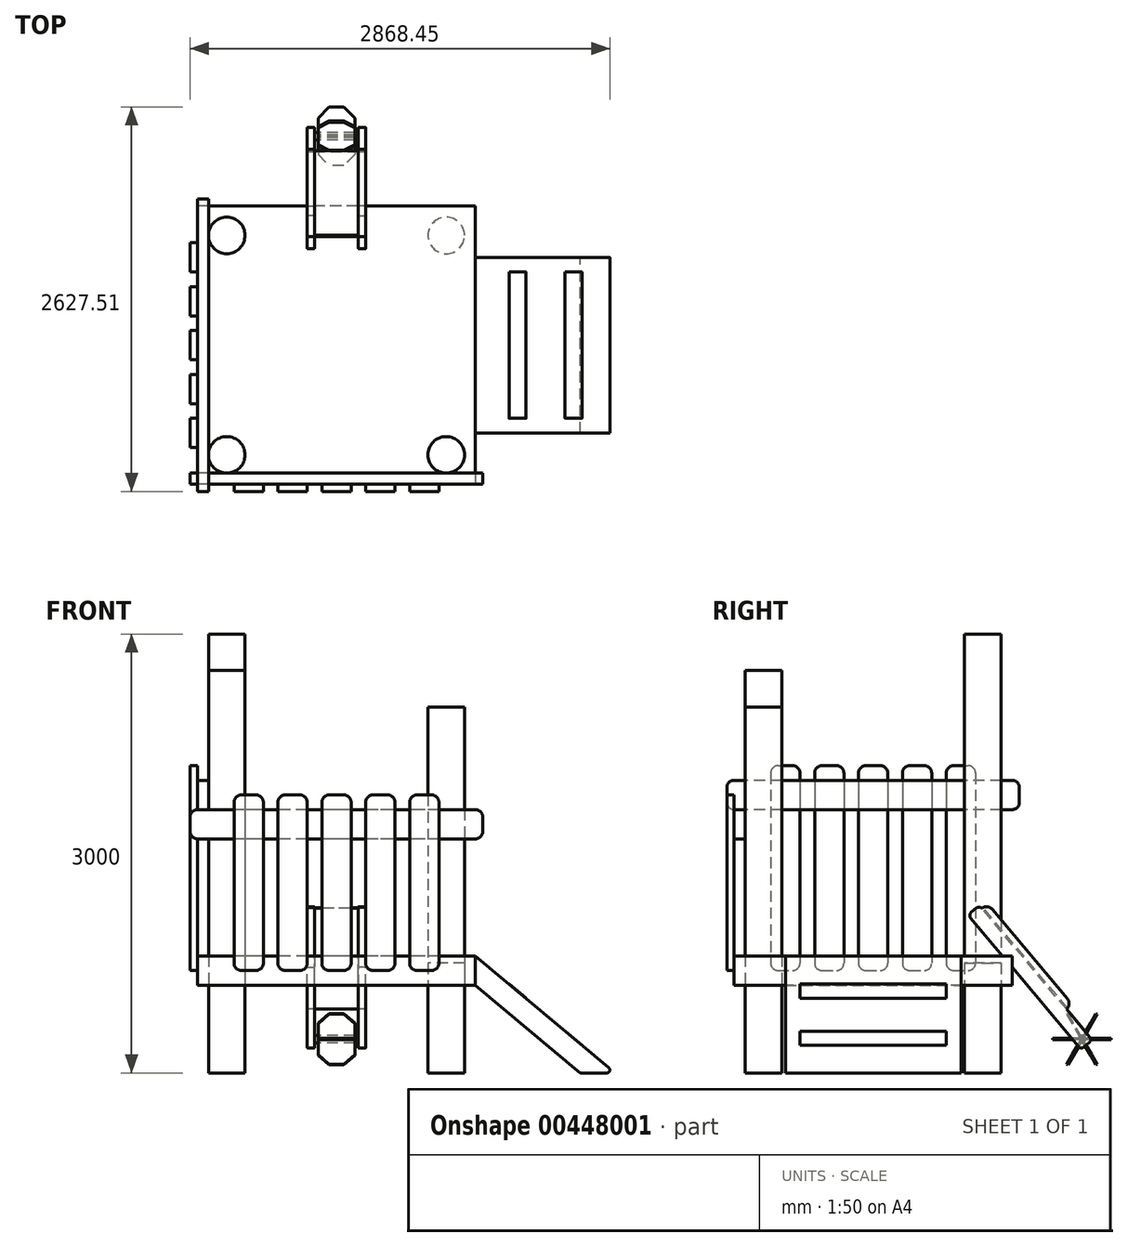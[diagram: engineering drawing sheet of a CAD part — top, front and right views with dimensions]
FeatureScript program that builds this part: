
annotation { "Feature Type Name" : "Feature", "Feature Type Description" : "" }
export const myFeature = defineFeature(function(context is Context, id is Id, definition is map)
    precondition{}
    {
        {
            var Q0;
            Q0=qCreatedBy(makeId("Top.planeOp"),FACE);
            var sketch = newSketch(context, id + "F0", { "sketchPlane" : qUnion([Q0])});
            skLineSegment(sketch, "E0.bottom", {"start": v(750, 750) * mm, "end": v(-750, 750) * mm, "construction": true});
            skLineSegment(sketch, "E0.top", {"start": v(750, -750) * mm, "end": v(-750, -750) * mm, "construction": true});
            skLineSegment(sketch, "E0.left", {"start": v(750, 750) * mm, "end": v(750, -750) * mm, "construction": true});
            skLineSegment(sketch, "E0.right", {"start": v(-750, 750) * mm, "end": v(-750, -750) * mm, "construction": true});
            skPoint(sketch, "E0.middle", {"position": v(0, 0) * mm});
            skCircle(sketch, "E1", {"center": v(-750, 750) * mm, "radius": 125 * mm});
            skCircle(sketch, "E2", {"center": v(750, 750) * mm, "radius": 125 * mm});
            skCircle(sketch, "E3", {"center": v(750, -750) * mm, "radius": 125 * mm});
            skCircle(sketch, "E4", {"center": v(-750, -750) * mm, "radius": 125 * mm});
            skSolve(sketch);
        }
        {
            var Q0;
            Q0=qCreatedBy(makeId("Top.planeOp"),FACE);
            cPlane(context, id + "F1", {"entities" : qUnion([Q0]), "cplaneType" : CPlaneType.OFFSET, "offset" : 800 * mm, "width" : 150 * mm, "height" : 150 * mm});
        }
        {
            var Q0;
            Q0=qCreatedBy(id+"F1.planeOp",FACE);
            var sketch = newSketch(context, id + "F2", { "sketchPlane" : qUnion([Q0])});
            skLineSegment(sketch, "E5.bottom", {"start": v(950, 950) * mm, "end": v(-950, 950) * mm});
            skLineSegment(sketch, "E5.top", {"start": v(950, -950) * mm, "end": v(-950, -950) * mm});
            skLineSegment(sketch, "E5.left", {"start": v(950, 950) * mm, "end": v(950, -950) * mm});
            skLineSegment(sketch, "E5.right", {"start": v(-950, 950) * mm, "end": v(-950, -950) * mm});
            skPoint(sketch, "E5.middle", {"position": v(0, 0) * mm});
            skSolve(sketch);
        }
        {
            var Q0;
            Q0=makeQuery(id+"F0.imprint","IMPRINT",FACE,{"disambiguationData":[TD([[makeQuery(id+"F0.imprint","IMPRINT",EDGE,{"derivedFrom":sQuery(id+"F0.wireOp",EDGE,"E1")}),1.0]])]});
            var Q1;
            Q1=sQuery(id+"F0.wireOp",EDGE,"E1");
            extrude(context, id + "F3", {"entities" : qUnion([Q0]), "surfaceEntities" : qUnion([Q1]), "depth" : 3000 * mm});
        }
        {
            var Q0;
            Q0=makeQuery(id+"F0.imprint","IMPRINT",FACE,{"disambiguationData":[TD([[makeQuery(id+"F0.imprint","IMPRINT",EDGE,{"derivedFrom":sQuery(id+"F0.wireOp",EDGE,"E4")}),1.0]])]});
            var Q1;
            Q1=sQuery(id+"F0.wireOp",EDGE,"E4");
            extrude(context, id + "F4", {"entities" : qUnion([Q0]), "surfaceEntities" : qUnion([Q1]), "depth" : 2750 * mm});
        }
        {
            var Q0;
            Q0=makeQuery(id+"F0.imprint","IMPRINT",FACE,{"disambiguationData":[TD([[makeQuery(id+"F0.imprint","IMPRINT",EDGE,{"derivedFrom":sQuery(id+"F0.wireOp",EDGE,"E3")}),1.0]])]});
            extrude(context, id + "F5", {"entities" : qUnion([Q0]), "depth" : 2500 * mm});
        }
        {
            var Q0;
            Q0=makeQuery(id+"F0.imprint","IMPRINT",FACE,{"disambiguationData":[TD([[makeQuery(id+"F0.imprint","IMPRINT",EDGE,{"derivedFrom":sQuery(id+"F0.wireOp",EDGE,"E2")}),1.0]])]});
            var Q1;
            Q1=sQuery(id+"F0.wireOp",EDGE,"E2");
            extrude(context, id + "F6", {"entities" : qUnion([Q0]), "surfaceEntities" : qUnion([Q1]), "depth" : 750 * mm});
        }
        {
            var Q0;
            Q0=makeQuery(id+"F2.imprint","IMPRINT",FACE,{"disambiguationData":[TD([[makeQuery(id+"F2.imprint","IMPRINT",EDGE,{"derivedFrom":sQuery(id+"F2.wireOp",EDGE,"E5.bottom")}),1.0]])]});
            extrude(context, id + "F7", {"entities" : qUnion([Q0]), "oppositeDirection" : true, "depth" : 200 * mm});
        }
        {
            var Q0;
            Q0=makeQuery(id+"F2.imprint","IMPRINT",FACE,{"disambiguationData":[TD([[makeQuery(id+"F2.imprint","IMPRINT",EDGE,{"derivedFrom":sQuery(id+"F2.wireOp",EDGE,"E5.bottom")}),1.0]])]});
            cPlane(context, id + "F8", {"entities" : qUnion([Q0]), "cplaneType" : CPlaneType.OFFSET, "offset" : 1000 * mm, "width" : 150 * mm, "height" : 150 * mm});
        }
        {
            var Q0;
            Q0=qCreatedBy(id+"F8.planeOp",FACE);
            var sketch = newSketch(context, id + "F9", { "sketchPlane" : qUnion([Q0])});
            skLineSegment(sketch, "E6.bottom", {"start": v(1000, -950) * mm, "end": v(-1000, -950) * mm});
            skLineSegment(sketch, "E6.top", {"start": v(1000, -875) * mm, "end": v(-1000, -875) * mm});
            skLineSegment(sketch, "E6.left", {"start": v(1000, -950) * mm, "end": v(1000, -875) * mm});
            skLineSegment(sketch, "E6.right", {"start": v(-1000, -950) * mm, "end": v(-1000, -875) * mm});
            skPoint(sketch, "E6.middle", {"position": v(0, -912.5) * mm});
            skLineSegment(sketch, "E7.bottom", {"start": v(-950, 1000) * mm, "end": v(-875, 1000) * mm});
            skLineSegment(sketch, "E7.top", {"start": v(-950, -1000) * mm, "end": v(-875, -1000) * mm});
            skLineSegment(sketch, "E7.left", {"start": v(-950, 1000) * mm, "end": v(-950, -1000) * mm});
            skLineSegment(sketch, "E7.right", {"start": v(-875, 1000) * mm, "end": v(-875, -1000) * mm});
            skPoint(sketch, "E7.middle", {"position": v(-912.5, 0) * mm});
            skSolve(sketch);
        }
        {
            var Q0;
            {var subQ5=sQuery(id+"F9.wireOp",EDGE,"E7.bottom");Q0=makeQuery(id+"F9.imprint","IMPRINT",FACE,{"disambiguationData":[TD([[makeQuery(id+"F9.imprint","IMPRINT",EDGE,{"derivedFrom":subQ5}),-1.0]])]});}
            var Q1;
            {var subQ0=sQuery(id+"F9.wireOp",EDGE,"E7.right");var subQ1=sQuery(id+"F9.wireOp",EDGE,"E6.bottom");var subQ2=makeQuery(id+"F9.imprint","INTERSECT",VERTEX,{"derivedFrom":[subQ1,subQ0]});Q1=makeQuery(id+"F9.imprint","IMPRINT",FACE,{"disambiguationData":[TD([[makeQuery(id+"F9.imprint","IMPRINT",EDGE,{"disambiguationData":[TD([[subQ2,-1.0]])],"derivedFrom":subQ1}),-1.0]])]});}
            var Q2;
            {var subQ5=sQuery(id+"F9.wireOp",EDGE,"E7.top");Q2=makeQuery(id+"F9.imprint","IMPRINT",FACE,{"disambiguationData":[TD([[makeQuery(id+"F9.imprint","IMPRINT",EDGE,{"derivedFrom":subQ5}),1.0]])]});}
            extrude(context, id + "F10", {"entities" : qUnion([Q0, Q1, Q2]), "operationType" : NewBodyOperationType.ADD, "depth" : 200 * mm});
        }
        {
            var Q0;
            {var subQ0=sQuery(id+"F9.wireOp",EDGE,"E6.right");Q0=makeQuery(id+"F9.imprint","IMPRINT",FACE,{"disambiguationData":[TD([[makeQuery(id+"F9.imprint","IMPRINT",EDGE,{"derivedFrom":subQ0}),-1.0]])]});}
            var Q1;
            {var subQ0=sQuery(id+"F9.wireOp",EDGE,"E7.right");var subQ1=sQuery(id+"F9.wireOp",EDGE,"E6.bottom");var subQ2=makeQuery(id+"F9.imprint","INTERSECT",VERTEX,{"derivedFrom":[subQ1,subQ0]});Q1=makeQuery(id+"F9.imprint","IMPRINT",FACE,{"disambiguationData":[TD([[makeQuery(id+"F9.imprint","IMPRINT",EDGE,{"disambiguationData":[TD([[subQ2,-1.0]])],"derivedFrom":subQ1}),-1.0]])]});}
            var Q2;
            {var subQ0=sQuery(id+"F9.wireOp",EDGE,"E6.left");Q2=makeQuery(id+"F9.imprint","IMPRINT",FACE,{"disambiguationData":[TD([[makeQuery(id+"F9.imprint","IMPRINT",EDGE,{"derivedFrom":subQ0}),1.0]])]});}
            extrude(context, id + "F11", {"entities" : qUnion([Q0, Q1, Q2]), "depth" : -200 * mm});
        }
        {
            var Q0;
            Q0=makeQuery(id+"F2.imprint","IMPRINT",FACE,{"disambiguationData":[TD([[makeQuery(id+"F2.imprint","IMPRINT",EDGE,{"derivedFrom":sQuery(id+"F2.wireOp",EDGE,"E5.bottom")}),1.0]])]});
            cPlane(context, id + "F12", {"entities" : qUnion([Q0]), "cplaneType" : CPlaneType.OFFSET, "offset" : 500 * mm, "width" : 150 * mm, "height" : 150 * mm});
        }
        {
            var Q0;
            Q0=qCreatedBy(id+"F12.planeOp",FACE);
            var Q1;
            Q1=qCreatedBy(id+"F12.planeOp",FACE);
            var sketch = newSketch(context, id + "F13", { "sketchPlane" : qUnion([Q0, Q1])});
            skLineSegment(sketch, "E8.bottom", {"start": v(100, -1000) * mm, "end": v(-100, -1000) * mm});
            skLineSegment(sketch, "E8.top", {"start": v(100, -950) * mm, "end": v(-100, -950) * mm});
            skLineSegment(sketch, "E8.left", {"start": v(100, -1000) * mm, "end": v(100, -950) * mm});
            skLineSegment(sketch, "E8.right", {"start": v(-100, -1000) * mm, "end": v(-100, -950) * mm});
            skPoint(sketch, "E8.middle", {"position": v(0, -950) * mm});
            skLineSegment(sketch, "E9.1.0.0", {"start": v(400, -1000) * mm, "end": v(400, -950) * mm});
            skLineSegment(sketch, "E9.1.0.1", {"start": v(400, -950) * mm, "end": v(200, -950) * mm});
            skLineSegment(sketch, "E9.1.0.2", {"start": v(400, -1000) * mm, "end": v(200, -1000) * mm});
            skPoint(sketch, "E9.1.0.3", {"position": v(300, -950) * mm});
            skLineSegment(sketch, "E9.1.0.4", {"start": v(200, -1000) * mm, "end": v(200, -950) * mm});
            skLineSegment(sketch, "E9.2.0.0", {"start": v(700, -1000) * mm, "end": v(700, -950) * mm});
            skLineSegment(sketch, "E9.2.0.1", {"start": v(700, -950) * mm, "end": v(500, -950) * mm});
            skLineSegment(sketch, "E9.2.0.2", {"start": v(700, -1000) * mm, "end": v(500, -1000) * mm});
            skPoint(sketch, "E9.2.0.3", {"position": v(600, -950) * mm});
            skLineSegment(sketch, "E9.2.0.4", {"start": v(500, -1000) * mm, "end": v(500, -950) * mm});
            skLineSegment(sketch, "E9.direction1", {"start": v(-100, -1000) * mm, "end": v(200, -1000) * mm, "construction": true});
            skLineSegment(sketch, "E10.1.0.0", {"start": v(-200, -1000) * mm, "end": v(-400, -1000) * mm});
            skLineSegment(sketch, "E10.1.0.1", {"start": v(-200, -950) * mm, "end": v(-400, -950) * mm});
            skLineSegment(sketch, "E10.1.0.2", {"start": v(-200, -1000) * mm, "end": v(-200, -950) * mm});
            skLineSegment(sketch, "E10.1.0.3", {"start": v(-400, -1000) * mm, "end": v(-400, -950) * mm});
            skPoint(sketch, "E10.1.0.4", {"position": v(-300, -950) * mm});
            skLineSegment(sketch, "E10.2.0.0", {"start": v(-500, -1000) * mm, "end": v(-700, -1000) * mm});
            skLineSegment(sketch, "E10.2.0.1", {"start": v(-500, -950) * mm, "end": v(-700, -950) * mm});
            skLineSegment(sketch, "E10.2.0.2", {"start": v(-500, -1000) * mm, "end": v(-500, -950) * mm});
            skLineSegment(sketch, "E10.2.0.3", {"start": v(-700, -1000) * mm, "end": v(-700, -950) * mm});
            skPoint(sketch, "E10.2.0.4", {"position": v(-600, -950) * mm});
            skLineSegment(sketch, "E10.direction1", {"start": v(-100, -1000) * mm, "end": v(-400, -1000) * mm, "construction": true});
            skSolve(sketch);
        }
        {
            var Q0;
            Q0=makeQuery(id+"F13.imprint","IMPRINT",FACE,{"disambiguationData":[TD([[makeQuery(id+"F13.imprint","IMPRINT",EDGE,{"derivedFrom":sQuery(id+"F13.wireOp",EDGE,"E10.2.0.0")}),-1.0]])]});
            var Q1;
            Q1=makeQuery(id+"F13.imprint","IMPRINT",FACE,{"disambiguationData":[TD([[makeQuery(id+"F13.imprint","IMPRINT",EDGE,{"derivedFrom":sQuery(id+"F13.wireOp",EDGE,"E10.1.0.0")}),-1.0]])]});
            var Q2;
            Q2=makeQuery(id+"F13.imprint","IMPRINT",FACE,{"disambiguationData":[TD([[makeQuery(id+"F13.imprint","IMPRINT",EDGE,{"derivedFrom":sQuery(id+"F13.wireOp",EDGE,"E8.bottom")}),-1.0]])]});
            var Q3;
            Q3=makeQuery(id+"F13.imprint","IMPRINT",FACE,{"disambiguationData":[TD([[makeQuery(id+"F13.imprint","IMPRINT",EDGE,{"derivedFrom":sQuery(id+"F13.wireOp",EDGE,"E9.1.0.0")}),1.0]])]});
            var Q4;
            Q4=makeQuery(id+"F13.imprint","IMPRINT",FACE,{"disambiguationData":[TD([[makeQuery(id+"F13.imprint","IMPRINT",EDGE,{"derivedFrom":sQuery(id+"F13.wireOp",EDGE,"E9.2.0.0")}),1.0]])]});
            extrude(context, id + "F14", {"entities" : qUnion([Q0, Q1, Q2, Q3, Q4]), "operationType" : NewBodyOperationType.ADD, "endBound" : BoundingType.SYMMETRIC, "depth" : 1200 * mm});
        }
        {
            var Q0;
            Q0=makeQuery(id+"F2.imprint","IMPRINT",FACE,{"disambiguationData":[TD([[makeQuery(id+"F2.imprint","IMPRINT",EDGE,{"derivedFrom":sQuery(id+"F2.wireOp",EDGE,"E5.bottom")}),1.0]])]});
            cPlane(context, id + "F15", {"entities" : qUnion([Q0]), "cplaneType" : CPlaneType.OFFSET, "offset" : 600 * mm, "width" : 150 * mm, "height" : 150 * mm});
        }
        {
            var Q0;
            Q0=qCreatedBy(id+"F15.planeOp",FACE);
            var sketch = newSketch(context, id + "F16", { "sketchPlane" : qUnion([Q0])});
            skLineSegment(sketch, "E11.bottom", {"start": v(-1000, -100) * mm, "end": v(-950, -100) * mm});
            skLineSegment(sketch, "E11.top", {"start": v(-1000, 100) * mm, "end": v(-950, 100) * mm});
            skLineSegment(sketch, "E11.left", {"start": v(-1000, -100) * mm, "end": v(-1000, 100) * mm});
            skLineSegment(sketch, "E11.right", {"start": v(-950, -100) * mm, "end": v(-950, 100) * mm});
            skPoint(sketch, "E11.middle", {"position": v(-975, 0) * mm});
            skLineSegment(sketch, "E12.0.1.0", {"start": v(-1000, 400) * mm, "end": v(-950, 400) * mm});
            skPoint(sketch, "E12.0.1.1", {"position": v(-975, 300) * mm});
            skLineSegment(sketch, "E12.0.1.2", {"start": v(-1000, 200) * mm, "end": v(-950, 200) * mm});
            skLineSegment(sketch, "E12.0.1.3", {"start": v(-950, 200) * mm, "end": v(-950, 400) * mm});
            skLineSegment(sketch, "E12.0.1.4", {"start": v(-1000, 200) * mm, "end": v(-1000, 400) * mm});
            skLineSegment(sketch, "E12.0.2.0", {"start": v(-1000, 700) * mm, "end": v(-950, 700) * mm});
            skPoint(sketch, "E12.0.2.1", {"position": v(-975, 600) * mm});
            skLineSegment(sketch, "E12.0.2.2", {"start": v(-1000, 500) * mm, "end": v(-950, 500) * mm});
            skLineSegment(sketch, "E12.0.2.3", {"start": v(-950, 500) * mm, "end": v(-950, 700) * mm});
            skLineSegment(sketch, "E12.0.2.4", {"start": v(-1000, 500) * mm, "end": v(-1000, 700) * mm});
            skLineSegment(sketch, "E12.direction1", {"start": v(-1000, -100) * mm, "end": v(-975, -100) * mm, "construction": true});
            skLineSegment(sketch, "E12.direction2", {"start": v(-1000, -100) * mm, "end": v(-1000, 200) * mm, "construction": true});
            skPoint(sketch, "E13.0.1.0", {"position": v(-975, -300) * mm});
            skLineSegment(sketch, "E13.0.1.1", {"start": v(-950, -400) * mm, "end": v(-950, -200) * mm});
            skLineSegment(sketch, "E13.0.1.2", {"start": v(-1000, -400) * mm, "end": v(-1000, -200) * mm});
            skLineSegment(sketch, "E13.0.1.3", {"start": v(-1000, -200) * mm, "end": v(-950, -200) * mm});
            skLineSegment(sketch, "E13.0.1.4", {"start": v(-1000, -400) * mm, "end": v(-975, -400) * mm, "construction": true});
            skLineSegment(sketch, "E13.0.1.5", {"start": v(-1000, -400) * mm, "end": v(-950, -400) * mm});
            skPoint(sketch, "E13.0.2.0", {"position": v(-975, -600) * mm});
            skLineSegment(sketch, "E13.0.2.1", {"start": v(-950, -700) * mm, "end": v(-950, -500) * mm});
            skLineSegment(sketch, "E13.0.2.2", {"start": v(-1000, -700) * mm, "end": v(-1000, -500) * mm});
            skLineSegment(sketch, "E13.0.2.3", {"start": v(-1000, -500) * mm, "end": v(-950, -500) * mm});
            skLineSegment(sketch, "E13.0.2.4", {"start": v(-1000, -700) * mm, "end": v(-975, -700) * mm, "construction": true});
            skLineSegment(sketch, "E13.0.2.5", {"start": v(-1000, -700) * mm, "end": v(-950, -700) * mm});
            skLineSegment(sketch, "E13.direction2", {"start": v(-1000, -100) * mm, "end": v(-1000, -400) * mm, "construction": true});
            skSolve(sketch);
        }
        {
            var Q0;
            Q0=makeQuery(id+"F16.imprint","IMPRINT",FACE,{"disambiguationData":[TD([[makeQuery(id+"F16.imprint","IMPRINT",EDGE,{"derivedFrom":sQuery(id+"F16.wireOp",EDGE,"E13.0.2.1")}),1.0]])]});
            var Q1;
            Q1=makeQuery(id+"F16.imprint","IMPRINT",FACE,{"disambiguationData":[TD([[makeQuery(id+"F16.imprint","IMPRINT",EDGE,{"derivedFrom":sQuery(id+"F16.wireOp",EDGE,"E13.0.1.1")}),1.0]])]});
            var Q2;
            Q2=makeQuery(id+"F16.imprint","IMPRINT",FACE,{"disambiguationData":[TD([[makeQuery(id+"F16.imprint","IMPRINT",EDGE,{"derivedFrom":sQuery(id+"F16.wireOp",EDGE,"E11.bottom")}),1.0]])]});
            var Q3;
            Q3=makeQuery(id+"F16.imprint","IMPRINT",FACE,{"disambiguationData":[TD([[makeQuery(id+"F16.imprint","IMPRINT",EDGE,{"derivedFrom":sQuery(id+"F16.wireOp",EDGE,"E12.0.2.0")}),-1.0]])]});
            var Q4;
            Q4=makeQuery(id+"F16.imprint","IMPRINT",FACE,{"disambiguationData":[TD([[makeQuery(id+"F16.imprint","IMPRINT",EDGE,{"derivedFrom":sQuery(id+"F16.wireOp",EDGE,"E12.0.1.0")}),-1.0]])]});
            extrude(context, id + "F17", {"entities" : qUnion([Q0, Q1, Q2, Q3, Q4]), "endBound" : BoundingType.SYMMETRIC, "depth" : 1400 * mm});
        }
        {
            var Q0;
            Q0=makeQuery(id+"F10.opExtrude","CAP_EDGE",EDGE,{"disambiguationData":[OSD([sQuery(id+"F9.wireOp",EDGE,"E7.top")])],"isStart":false});
            var Q1;
            Q1=makeQuery(id+"F10.opExtrude","CAP_EDGE",EDGE,{"disambiguationData":[OSD([sQuery(id+"F9.wireOp",EDGE,"E7.top")])],"isStart":true});
            var Q2;
            Q2=makeQuery(id+"F10.opExtrude","CAP_EDGE",EDGE,{"disambiguationData":[OSD([sQuery(id+"F9.wireOp",EDGE,"E7.bottom")])],"isStart":false});
            var Q3;
            Q3=makeQuery(id+"F10.opExtrude","CAP_EDGE",EDGE,{"disambiguationData":[OSD([sQuery(id+"F9.wireOp",EDGE,"E7.bottom")])],"isStart":true});
            var Q4;
            Q4=makeQuery(id+"F11.opExtrude","CAP_EDGE",EDGE,{"disambiguationData":[OSD([sQuery(id+"F9.wireOp",EDGE,"E6.right")])],"isStart":true});
            var Q5;
            Q5=makeQuery(id+"F11.opExtrude","CAP_EDGE",EDGE,{"disambiguationData":[OSD([sQuery(id+"F9.wireOp",EDGE,"E6.right")])],"isStart":false});
            var Q6;
            Q6=makeQuery(id+"F11.opExtrude","CAP_EDGE",EDGE,{"disambiguationData":[OSD([sQuery(id+"F9.wireOp",EDGE,"E6.left")])],"isStart":true});
            var Q7;
            Q7=makeQuery(id+"F11.opExtrude","CAP_EDGE",EDGE,{"disambiguationData":[OSD([sQuery(id+"F9.wireOp",EDGE,"E6.left")])],"isStart":false});
            var Q8;
            Q8=makeQuery(id+"F14.opExtrude","CAP_EDGE",EDGE,{"disambiguationData":[OSD([sQuery(id+"F13.wireOp",EDGE,"E10.2.0.3")])],"isStart":false});
            var Q9;
            Q9=makeQuery(id+"F14.opExtrude","CAP_EDGE",EDGE,{"disambiguationData":[OSD([sQuery(id+"F13.wireOp",EDGE,"E10.2.0.2")])],"isStart":false});
            var Q10;
            Q10=makeQuery(id+"F14.opExtrude","CAP_EDGE",EDGE,{"disambiguationData":[OSD([sQuery(id+"F13.wireOp",EDGE,"E10.1.0.3")])],"isStart":false});
            var Q11;
            Q11=makeQuery(id+"F14.opExtrude","CAP_EDGE",EDGE,{"disambiguationData":[OSD([sQuery(id+"F13.wireOp",EDGE,"E10.1.0.2")])],"isStart":false});
            var Q12;
            Q12=makeQuery(id+"F14.opExtrude","CAP_EDGE",EDGE,{"disambiguationData":[OSD([sQuery(id+"F13.wireOp",EDGE,"E8.right")])],"isStart":false});
            var Q13;
            Q13=makeQuery(id+"F14.opExtrude","CAP_EDGE",EDGE,{"disambiguationData":[OSD([sQuery(id+"F13.wireOp",EDGE,"E8.left")])],"isStart":false});
            var Q14;
            Q14=makeQuery(id+"F14.opExtrude","CAP_EDGE",EDGE,{"disambiguationData":[OSD([sQuery(id+"F13.wireOp",EDGE,"E9.1.0.4")])],"isStart":false});
            var Q15;
            Q15=makeQuery(id+"F14.opExtrude","CAP_EDGE",EDGE,{"disambiguationData":[OSD([sQuery(id+"F13.wireOp",EDGE,"E9.1.0.0")])],"isStart":false});
            var Q16;
            Q16=makeQuery(id+"F14.opExtrude","CAP_EDGE",EDGE,{"disambiguationData":[OSD([sQuery(id+"F13.wireOp",EDGE,"E9.2.0.4")])],"isStart":false});
            var Q17;
            Q17=makeQuery(id+"F14.opExtrude","CAP_EDGE",EDGE,{"disambiguationData":[OSD([sQuery(id+"F13.wireOp",EDGE,"E9.2.0.0")])],"isStart":false});
            var Q18;
            Q18=makeQuery(id+"F14.opExtrude","CAP_EDGE",EDGE,{"disambiguationData":[OSD([sQuery(id+"F13.wireOp",EDGE,"E10.2.0.3")])],"isStart":true});
            var Q19;
            Q19=makeQuery(id+"F14.opExtrude","CAP_EDGE",EDGE,{"disambiguationData":[OSD([sQuery(id+"F13.wireOp",EDGE,"E10.2.0.2")])],"isStart":true});
            var Q20;
            Q20=makeQuery(id+"F14.opExtrude","CAP_EDGE",EDGE,{"disambiguationData":[OSD([sQuery(id+"F13.wireOp",EDGE,"E10.1.0.3")])],"isStart":true});
            var Q21;
            Q21=makeQuery(id+"F14.opExtrude","CAP_EDGE",EDGE,{"disambiguationData":[OSD([sQuery(id+"F13.wireOp",EDGE,"E10.1.0.2")])],"isStart":true});
            var Q22;
            Q22=makeQuery(id+"F14.opExtrude","CAP_EDGE",EDGE,{"disambiguationData":[OSD([sQuery(id+"F13.wireOp",EDGE,"E8.right")])],"isStart":true});
            var Q23;
            Q23=makeQuery(id+"F14.opExtrude","CAP_EDGE",EDGE,{"disambiguationData":[OSD([sQuery(id+"F13.wireOp",EDGE,"E8.left")])],"isStart":true});
            var Q24;
            Q24=makeQuery(id+"F14.opExtrude","CAP_EDGE",EDGE,{"disambiguationData":[OSD([sQuery(id+"F13.wireOp",EDGE,"E9.1.0.4")])],"isStart":true});
            var Q25;
            Q25=makeQuery(id+"F14.opExtrude","CAP_EDGE",EDGE,{"disambiguationData":[OSD([sQuery(id+"F13.wireOp",EDGE,"E9.1.0.0")])],"isStart":true});
            var Q26;
            Q26=makeQuery(id+"F14.opExtrude","CAP_EDGE",EDGE,{"disambiguationData":[OSD([sQuery(id+"F13.wireOp",EDGE,"E9.2.0.4")])],"isStart":true});
            var Q27;
            Q27=makeQuery(id+"F14.opExtrude","CAP_EDGE",EDGE,{"disambiguationData":[OSD([sQuery(id+"F13.wireOp",EDGE,"E9.2.0.0")])],"isStart":true});
            var Q28;
            Q28=makeQuery(id+"F17.opExtrude","CAP_EDGE",EDGE,{"disambiguationData":[OSD([sQuery(id+"F16.wireOp",EDGE,"E12.0.2.0")])],"isStart":false});
            var Q29;
            Q29=makeQuery(id+"F17.opExtrude","CAP_EDGE",EDGE,{"disambiguationData":[OSD([sQuery(id+"F16.wireOp",EDGE,"E12.0.2.2")])],"isStart":false});
            var Q30;
            Q30=makeQuery(id+"F17.opExtrude","CAP_EDGE",EDGE,{"disambiguationData":[OSD([sQuery(id+"F16.wireOp",EDGE,"E12.0.1.0")])],"isStart":false});
            var Q31;
            Q31=makeQuery(id+"F17.opExtrude","CAP_EDGE",EDGE,{"disambiguationData":[OSD([sQuery(id+"F16.wireOp",EDGE,"E12.0.1.2")])],"isStart":false});
            var Q32;
            Q32=makeQuery(id+"F17.opExtrude","CAP_EDGE",EDGE,{"disambiguationData":[OSD([sQuery(id+"F16.wireOp",EDGE,"E11.top")])],"isStart":false});
            var Q33;
            Q33=makeQuery(id+"F17.opExtrude","CAP_EDGE",EDGE,{"disambiguationData":[OSD([sQuery(id+"F16.wireOp",EDGE,"E11.bottom")])],"isStart":false});
            var Q34;
            Q34=makeQuery(id+"F17.opExtrude","CAP_EDGE",EDGE,{"disambiguationData":[OSD([sQuery(id+"F16.wireOp",EDGE,"E13.0.1.3")])],"isStart":false});
            var Q35;
            Q35=makeQuery(id+"F17.opExtrude","CAP_EDGE",EDGE,{"disambiguationData":[OSD([sQuery(id+"F16.wireOp",EDGE,"E13.0.1.5")])],"isStart":false});
            var Q36;
            Q36=makeQuery(id+"F17.opExtrude","CAP_EDGE",EDGE,{"disambiguationData":[OSD([sQuery(id+"F16.wireOp",EDGE,"E13.0.2.3")])],"isStart":false});
            var Q37;
            Q37=makeQuery(id+"F17.opExtrude","CAP_EDGE",EDGE,{"disambiguationData":[OSD([sQuery(id+"F16.wireOp",EDGE,"E13.0.2.5")])],"isStart":false});
            var Q38;
            Q38=makeQuery(id+"F17.opExtrude","CAP_EDGE",EDGE,{"disambiguationData":[OSD([sQuery(id+"F16.wireOp",EDGE,"E13.0.2.5")])],"isStart":true});
            var Q39;
            Q39=makeQuery(id+"F17.opExtrude","CAP_EDGE",EDGE,{"disambiguationData":[OSD([sQuery(id+"F16.wireOp",EDGE,"E13.0.2.3")])],"isStart":true});
            var Q40;
            Q40=makeQuery(id+"F17.opExtrude","CAP_EDGE",EDGE,{"disambiguationData":[OSD([sQuery(id+"F16.wireOp",EDGE,"E13.0.1.5")])],"isStart":true});
            var Q41;
            Q41=makeQuery(id+"F17.opExtrude","CAP_EDGE",EDGE,{"disambiguationData":[OSD([sQuery(id+"F16.wireOp",EDGE,"E13.0.1.3")])],"isStart":true});
            var Q42;
            Q42=makeQuery(id+"F17.opExtrude","CAP_EDGE",EDGE,{"disambiguationData":[OSD([sQuery(id+"F16.wireOp",EDGE,"E11.bottom")])],"isStart":true});
            var Q43;
            Q43=makeQuery(id+"F17.opExtrude","CAP_EDGE",EDGE,{"disambiguationData":[OSD([sQuery(id+"F16.wireOp",EDGE,"E11.top")])],"isStart":true});
            var Q44;
            Q44=makeQuery(id+"F17.opExtrude","CAP_EDGE",EDGE,{"disambiguationData":[OSD([sQuery(id+"F16.wireOp",EDGE,"E12.0.1.2")])],"isStart":true});
            var Q45;
            Q45=makeQuery(id+"F17.opExtrude","CAP_EDGE",EDGE,{"disambiguationData":[OSD([sQuery(id+"F16.wireOp",EDGE,"E12.0.1.0")])],"isStart":true});
            var Q46;
            Q46=makeQuery(id+"F17.opExtrude","CAP_EDGE",EDGE,{"disambiguationData":[OSD([sQuery(id+"F16.wireOp",EDGE,"E12.0.2.2")])],"isStart":true});
            var Q47;
            Q47=makeQuery(id+"F17.opExtrude","CAP_EDGE",EDGE,{"disambiguationData":[OSD([sQuery(id+"F16.wireOp",EDGE,"E12.0.2.0")])],"isStart":true});
            fillet(context, id + "F18", {"entities" : qUnion([Q0, Q1, Q2, Q3, Q4, Q5, Q6, Q7, Q8, Q9, Q10, Q11, Q12, Q13, Q14, Q15, Q16, Q17, Q18, Q19, Q20, Q21, Q22, Q23, Q24, Q25, Q26, Q27, Q28, Q29, Q30, Q31, Q32, Q33, Q34, Q35, Q36, Q37, Q38, Q39, Q40, Q41, Q42, Q43, Q44, Q45, Q46, Q47]), "radius" : 50 * mm, "tangentPropagation" : true, "allowEdgeOverflow" : false});
        }
        {
            var Q0;
            Q0=qCreatedBy(makeId("Front.planeOp"),FACE);
            var sketch = newSketch(context, id + "F19", { "sketchPlane" : qUnion([Q0])});
            skLineSegment(sketch, "E14", {"start": v(950, 800) * mm, "end": v(1861.3, 35.32) * mm});
            skLineSegment(sketch, "E15", {"start": v(1848.45, 0) * mm, "end": v(1665.05, 0) * mm});
            skLineSegment(sketch, "E16", {"start": v(1665.05, 0) * mm, "end": v(950, 600) * mm});
            skLineSegment(sketch, "E17", {"start": v(950, 600) * mm, "end": v(950, 800) * mm});
            skPoint(sketch, "E18", {"position": v(950, 800) * mm});
            skPoint(sketch, "E19.visualSharp", {"position": v(1903.4, 0) * mm});
            skArc(sketch, "E19.filletArc", {"start": v(1848.45, 0) * mm, "mid": v(1867.25, 13.16) * mm, "end": v(1861.3, 35.32) * mm});
            skSolve(sketch);
        }
        {
            var Q0;
            Q0=makeQuery(id+"F19.imprint","IMPRINT",FACE,{"disambiguationData":[TD([[makeQuery(id+"F19.imprint","IMPRINT",EDGE,{"derivedFrom":sQuery(id+"F19.wireOp",EDGE,"E14")}),-1.0]])]});
            extrude(context, id + "F20", {"entities" : qUnion([Q0]), "operationType" : NewBodyOperationType.ADD, "endBound" : BoundingType.SYMMETRIC, "depth" : 1200 * mm});
        }
        {
            var Q0;
            Q0=makeQuery(id+"F20.opExtrude","SWEPT_FACE",FACE,{"disambiguationData":[OSD([sQuery(id+"F19.wireOp",EDGE,"E14")])]});
            var sketch = newSketch(context, id + "F21", { "sketchPlane" : qUnion([Q0])});
            skLineSegment(sketch, "E20.bottom", {"start": v(663.51, 500) * mm, "end": v(513.51, 500) * mm});
            skLineSegment(sketch, "E20.top", {"start": v(663.51, -500) * mm, "end": v(513.51, -500) * mm});
            skLineSegment(sketch, "E20.left", {"start": v(663.51, 500) * mm, "end": v(663.51, -500) * mm});
            skLineSegment(sketch, "E20.right", {"start": v(513.51, 500) * mm, "end": v(513.51, -500) * mm});
            skPoint(sketch, "E20.middle", {"position": v(588.51, 0) * mm});
            skLineSegment(sketch, "E21.bottom", {"start": v(1163.51, 500) * mm, "end": v(1013.51, 500) * mm});
            skLineSegment(sketch, "E21.top", {"start": v(1163.51, -500) * mm, "end": v(1013.51, -500) * mm});
            skLineSegment(sketch, "E21.left", {"start": v(1163.51, 500) * mm, "end": v(1163.51, -500) * mm});
            skLineSegment(sketch, "E21.right", {"start": v(1013.51, 500) * mm, "end": v(1013.51, -500) * mm});
            skPoint(sketch, "E21.middle", {"position": v(1088.51, 0) * mm});
            skSolve(sketch);
        }
        {
            var Q0;
            Q0=makeQuery(id+"F21.imprint","IMPRINT",FACE,{"disambiguationData":[TD([[makeQuery(id+"F21.imprint","IMPRINT",EDGE,{"derivedFrom":sQuery(id+"F21.wireOp",EDGE,"E20.bottom")}),1.0]])]});
            var Q1;
            Q1=makeQuery(id+"F21.imprint","IMPRINT",FACE,{"disambiguationData":[TD([[makeQuery(id+"F21.imprint","IMPRINT",EDGE,{"derivedFrom":sQuery(id+"F21.wireOp",EDGE,"E21.bottom")}),1.0]])]});
            extrude(context, id + "F22", {"entities" : qUnion([Q0, Q1]), "operationType" : NewBodyOperationType.ADD, "depth" : 15 / 20 * mm});
        }
        {
            var Q0;
            Q0=makeQuery(id+"F22.opExtrude","CAP_EDGE",EDGE,{"disambiguationData":[OSD([sQuery(id+"F21.wireOp",EDGE,"E20.left")])],"isStart":false});
            var Q1;
            Q1=makeQuery(id+"F22.opExtrude","CAP_EDGE",EDGE,{"disambiguationData":[OSD([sQuery(id+"F21.wireOp",EDGE,"E20.right")])],"isStart":false});
            var Q2;
            Q2=makeQuery(id+"F22.opExtrude","CAP_EDGE",EDGE,{"disambiguationData":[OSD([sQuery(id+"F21.wireOp",EDGE,"E21.right")])],"isStart":false});
            var Q3;
            Q3=makeQuery(id+"F22.opExtrude","CAP_EDGE",EDGE,{"disambiguationData":[OSD([sQuery(id+"F21.wireOp",EDGE,"E21.left")])],"isStart":false});
            fillet(context, id + "F23", {"entities" : qUnion([Q0, Q1, Q2, Q3]), "radius" : 15 / 20 * mm, "tangentPropagation" : true, "allowEdgeOverflow" : false});
        }
        {
            var Q0;
            Q0=qCreatedBy(makeId("Right.planeOp"),FACE);
            cPlane(context, id + "F24", {"entities" : qUnion([Q0]), "cplaneType" : CPlaneType.OFFSET, "offset" : 150 * mm, "width" : 150 * mm, "height" : 150 * mm});
        }
        {
            var Q0;
            Q0=qCreatedBy(makeId("Right.planeOp"),FACE);
            cPlane(context, id + "F25", {"entities" : qUnion([Q0]), "cplaneType" : CPlaneType.OFFSET, "offset" : 150 * mm, "oppositeDirection" : true, "width" : 150 * mm, "height" : 150 * mm});
        }
        {
            var Q0;
            Q0=qCreatedBy(id+"F24.planeOp",FACE);
            var sketch = newSketch(context, id + "F26", { "sketchPlane" : qUnion([Q0])});
            skLineSegment(sketch, "E22.bottom", {"start": v(1421.35, 160.49) * mm, "end": v(650, 1079.74) * mm});
            skLineSegment(sketch, "E22.top", {"start": v(1497.95, 224.77) * mm, "end": v(726.6, 1144.02) * mm});
            skLineSegment(sketch, "E22.left", {"start": v(1421.35, 160.49) * mm, "end": v(1497.95, 224.77) * mm});
            skLineSegment(sketch, "E22.right", {"start": v(650, 1079.74) * mm, "end": v(726.6, 1144.02) * mm});
            skPoint(sketch, "E22.middle", {"position": v(1073.97, 652.25) * mm});
            skSolve(sketch);
        }
        {
            var Q0;
            Q0=qCreatedBy(id+"F25.planeOp",FACE);
            var sketch = newSketch(context, id + "F27", { "sketchPlane" : qUnion([Q0])});
            skLineSegment(sketch, "E23.bottom", {"start": v(1421.35, 160.49) * mm, "end": v(650, 1079.74) * mm});
            skLineSegment(sketch, "E23.top", {"start": v(1497.95, 224.77) * mm, "end": v(726.6, 1144.02) * mm});
            skLineSegment(sketch, "E23.left", {"start": v(1421.35, 160.49) * mm, "end": v(1497.95, 224.77) * mm});
            skLineSegment(sketch, "E23.right", {"start": v(650, 1079.74) * mm, "end": v(726.6, 1144.02) * mm});
            skPoint(sketch, "E23.middle", {"position": v(1073.97, 652.25) * mm});
            skSolve(sketch);
        }
        {
            var Q0;
            Q0=qCreatedBy(makeId("Right.planeOp"),FACE);
            var sketch = newSketch(context, id + "F28", { "sketchPlane" : qUnion([Q0])});
            skLineSegment(sketch, "E24.bottom", {"start": v(1627.5, 225.93) * mm, "end": v(1227.5, 225.93) * mm});
            skLineSegment(sketch, "E24.top", {"start": v(1627.5, 235.93) * mm, "end": v(1227.5, 235.93) * mm});
            skLineSegment(sketch, "E24.left", {"start": v(1627.5, 225.93) * mm, "end": v(1627.5, 235.93) * mm});
            skLineSegment(sketch, "E24.right", {"start": v(1227.5, 225.93) * mm, "end": v(1227.5, 235.93) * mm});
            skPoint(sketch, "E24.middle", {"position": v(1427.5, 230.93) * mm});
            skLineSegment(sketch, "E25.bottom", {"start": v(1523.18, 55.22) * mm, "end": v(1323.18, 401.63) * mm});
            skLineSegment(sketch, "E25.top", {"start": v(1531.84, 60.22) * mm, "end": v(1331.84, 406.63) * mm});
            skLineSegment(sketch, "E25.left", {"start": v(1523.18, 55.22) * mm, "end": v(1531.84, 60.22) * mm});
            skLineSegment(sketch, "E25.right", {"start": v(1323.18, 401.63) * mm, "end": v(1331.84, 406.63) * mm});
            skLineSegment(sketch, "E26.bottom", {"start": v(1531.84, 401.63) * mm, "end": v(1331.84, 55.22) * mm});
            skLineSegment(sketch, "E26.top", {"start": v(1523.18, 406.63) * mm, "end": v(1323.18, 60.22) * mm});
            skLineSegment(sketch, "E26.left", {"start": v(1531.84, 401.63) * mm, "end": v(1523.18, 406.63) * mm});
            skLineSegment(sketch, "E26.right", {"start": v(1331.84, 55.22) * mm, "end": v(1323.18, 60.22) * mm});
            skSolve(sketch);
        }
        {
            var Q0;
            Q0=qCreatedBy(makeId("Right.planeOp"),FACE);
            var sketch = newSketch(context, id + "F29", { "sketchPlane" : qUnion([Q0])});
            skCircle(sketch, "E27", {"center": v(1427.5, 230.93) * mm, "radius": 25 * mm});
            skSolve(sketch);
        }
        {
            var Q0;
            Q0 = qSketchRegion(id + "F28", true);
            extrude(context, id + "F30", {"entities" : qUnion([Q0]), "endBound" : BoundingType.SYMMETRIC, "depth" : 250 * mm});
        }
        {
            var Q0;
            Q0=makeQuery(id+"F30.opExtrude","CAP_EDGE",EDGE,{"disambiguationData":[OSD([sQuery(id+"F28.wireOp",EDGE,"E26.left")])],"isStart":false});
            var Q1;
            Q1=makeQuery(id+"F30.opExtrude","CAP_EDGE",EDGE,{"disambiguationData":[OSD([sQuery(id+"F28.wireOp",EDGE,"E26.left")])],"isStart":true});
            var Q2;
            Q2=makeQuery(id+"F30.opExtrude","CAP_EDGE",EDGE,{"disambiguationData":[OSD([sQuery(id+"F28.wireOp",EDGE,"E24.left")])],"isStart":true});
            var Q3;
            Q3=makeQuery(id+"F30.opExtrude","CAP_EDGE",EDGE,{"disambiguationData":[OSD([sQuery(id+"F28.wireOp",EDGE,"E24.left")])],"isStart":false});
            var Q4;
            Q4=makeQuery(id+"F30.opExtrude","CAP_EDGE",EDGE,{"disambiguationData":[OSD([sQuery(id+"F28.wireOp",EDGE,"E25.left")])],"isStart":false});
            var Q5;
            Q5=makeQuery(id+"F30.opExtrude","CAP_EDGE",EDGE,{"disambiguationData":[OSD([sQuery(id+"F28.wireOp",EDGE,"E25.left")])],"isStart":true});
            var Q6;
            Q6=makeQuery(id+"F30.opExtrude","CAP_EDGE",EDGE,{"disambiguationData":[OSD([sQuery(id+"F28.wireOp",EDGE,"E26.right")])],"isStart":false});
            var Q7;
            Q7=makeQuery(id+"F30.opExtrude","CAP_EDGE",EDGE,{"disambiguationData":[OSD([sQuery(id+"F28.wireOp",EDGE,"E26.right")])],"isStart":true});
            var Q8;
            Q8=makeQuery(id+"F30.opExtrude","CAP_EDGE",EDGE,{"disambiguationData":[OSD([sQuery(id+"F28.wireOp",EDGE,"E24.right")])],"isStart":true});
            var Q9;
            Q9=makeQuery(id+"F30.opExtrude","CAP_EDGE",EDGE,{"disambiguationData":[OSD([sQuery(id+"F28.wireOp",EDGE,"E24.right")])],"isStart":false});
            var Q10;
            Q10=makeQuery(id+"F30.opExtrude","CAP_EDGE",EDGE,{"disambiguationData":[OSD([sQuery(id+"F28.wireOp",EDGE,"E25.right")])],"isStart":true});
            var Q11;
            Q11=makeQuery(id+"F30.opExtrude","CAP_EDGE",EDGE,{"disambiguationData":[OSD([sQuery(id+"F28.wireOp",EDGE,"E25.right")])],"isStart":false});
            chamfer(context, id + "F31", {"entities" : qUnion([Q0, Q1, Q2, Q3, Q4, Q5, Q6, Q7, Q8, Q9, Q10, Q11]), "width" : 75 * mm, "tangentPropagation" : true});
        }
        {
            var Q0;
            Q0 = qSketchRegion(id + "F26", true);
            extrude(context, id + "F32", {"entities" : qUnion([Q0]), "operationType" : NewBodyOperationType.ADD, "depth" : 50 * mm});
        }
        {
            var Q0;
            Q0 = qSketchRegion(id + "F27", true);
            extrude(context, id + "F33", {"entities" : qUnion([Q0]), "operationType" : NewBodyOperationType.ADD, "oppositeDirection" : true, "depth" : 50 * mm});
        }
        {
            var Q0;
            Q0=makeQuery(id+"F33.opExtrude","SWEPT_EDGE",EDGE,{"disambiguationData":[OSD([sQuery(id+"F27.wireOp",EDGE,"E23.top"),sQuery(id+"F27.wireOp",EDGE,"E23.left")])]});
            var Q1;
            Q1=makeQuery(id+"F33.opExtrude","SWEPT_EDGE",EDGE,{"disambiguationData":[OSD([sQuery(id+"F27.wireOp",EDGE,"E23.bottom"),sQuery(id+"F27.wireOp",EDGE,"E23.left")])]});
            var Q2;
            Q2=makeQuery(id+"F32.opExtrude","SWEPT_EDGE",EDGE,{"disambiguationData":[OSD([sQuery(id+"F26.wireOp",EDGE,"E22.top"),sQuery(id+"F26.wireOp",EDGE,"E22.left")])]});
            var Q3;
            Q3=makeQuery(id+"F32.opExtrude","SWEPT_EDGE",EDGE,{"disambiguationData":[OSD([sQuery(id+"F26.wireOp",EDGE,"E22.bottom"),sQuery(id+"F26.wireOp",EDGE,"E22.left")])]});
            var Q4;
            Q4=makeQuery(id+"F32.opExtrude","SWEPT_EDGE",EDGE,{"disambiguationData":[OSD([sQuery(id+"F26.wireOp",EDGE,"E22.top"),sQuery(id+"F26.wireOp",EDGE,"E22.right")])]});
            var Q5;
            Q5=makeQuery(id+"F32.opExtrude","SWEPT_EDGE",EDGE,{"disambiguationData":[OSD([sQuery(id+"F26.wireOp",EDGE,"E22.bottom"),sQuery(id+"F26.wireOp",EDGE,"E22.right")])]});
            var Q6;
            Q6=makeQuery(id+"F33.opExtrude","SWEPT_EDGE",EDGE,{"disambiguationData":[OSD([sQuery(id+"F27.wireOp",EDGE,"E23.bottom"),sQuery(id+"F27.wireOp",EDGE,"E23.right")])]});
            var Q7;
            Q7=makeQuery(id+"F33.opExtrude","SWEPT_EDGE",EDGE,{"disambiguationData":[OSD([sQuery(id+"F27.wireOp",EDGE,"E23.top"),sQuery(id+"F27.wireOp",EDGE,"E23.right")])]});
            fillet(context, id + "F34", {"entities" : qUnion([Q0, Q1, Q2, Q3, Q4, Q5, Q6, Q7]), "radius" : 25 * mm, "tangentPropagation" : true, "allowEdgeOverflow" : false});
        }
        {
            var Q0;
            Q0 = qSketchRegion(id + "F29", true);
            extrude(context, id + "F35", {"entities" : qUnion([Q0]), "endBound" : BoundingType.SYMMETRIC, "depth" : 300 * mm});
        }
        {
            var Q0;
            Q0=makeQuery(id+"F32.opExtrude","SWEPT_FACE",FACE,{"disambiguationData":[OSD([sQuery(id+"F26.wireOp",EDGE,"E22.top")])]});
            var sketch = newSketch(context, id + "F36", { "sketchPlane" : qUnion([Q0])});
            skLineSegment(sketch, "E28.bottom", {"start": v(-200, 384.32) * mm, "end": v(200, 384.32) * mm});
            skLineSegment(sketch, "E28.top", {"start": v(-200, -515.68) * mm, "end": v(200, -515.68) * mm});
            skLineSegment(sketch, "E28.left", {"start": v(-200, 384.32) * mm, "end": v(-200, -515.68) * mm});
            skLineSegment(sketch, "E28.right", {"start": v(200, 384.32) * mm, "end": v(200, -515.68) * mm});
            skSolve(sketch);
        }
        {
            var Q0;
            {var subQ4=sQuery(id+"F36.wireOp",EDGE,"E28.left");Q0=makeQuery(id+"F36.imprint","IMPRINT",FACE,{"disambiguationData":[TD([[makeQuery(id+"F36.imprint","IMPRINT",EDGE,{"derivedFrom":subQ4}),-1.0]])]});}
            var sketch = newSketch(context, id + "F37", { "sketchPlane" : qUnion([Q0])});
            skLineSegment(sketch, "E29.bottom", {"start": v(150, 384.32) * mm, "end": v(200, 384.32) * mm});
            skLineSegment(sketch, "E29.top", {"start": v(150, -515.68) * mm, "end": v(200, -515.68) * mm});
            skLineSegment(sketch, "E29.left", {"start": v(150, 384.32) * mm, "end": v(150, -515.68) * mm});
            skLineSegment(sketch, "E29.right", {"start": v(200, 384.32) * mm, "end": v(200, -515.68) * mm});
            skLineSegment(sketch, "E30.bottom", {"start": v(-200, 384.32) * mm, "end": v(-150, 384.32) * mm});
            skLineSegment(sketch, "E30.top", {"start": v(-200, -515.68) * mm, "end": v(-150, -515.68) * mm});
            skLineSegment(sketch, "E30.left", {"start": v(-200, 384.32) * mm, "end": v(-200, -515.68) * mm});
            skLineSegment(sketch, "E30.right", {"start": v(-150, 384.32) * mm, "end": v(-150, -515.68) * mm});
            skSolve(sketch);
        }
        {
            var Q0;
            Q0 = qSketchRegion(id + "F36", true);
            extrude(context, id + "F38", {"entities" : qUnion([Q0]), "operationType" : NewBodyOperationType.ADD, "depth" : 10 * mm});
        }
        {
            var Q0;
            Q0 = qSketchRegion(id + "F37", true);
            extrude(context, id + "F39", {"entities" : qUnion([Q0]), "operationType" : NewBodyOperationType.ADD, "depth" : 50 * mm});
        }
        {
            var Q0;
            Q0=makeQuery(id+"F39.opExtrude","CAP_EDGE",EDGE,{"disambiguationData":[OSD([sQuery(id+"F37.wireOp",EDGE,"E30.top")])],"isStart":false});
            var Q1;
            Q1=makeQuery(id+"F39.opExtrude","CAP_EDGE",EDGE,{"disambiguationData":[OSD([sQuery(id+"F37.wireOp",EDGE,"E29.top")])],"isStart":false});
            var Q2;
            Q2=makeQuery(id+"F39.opExtrude","CAP_EDGE",EDGE,{"disambiguationData":[OSD([sQuery(id+"F37.wireOp",EDGE,"E30.bottom")])],"isStart":false});
            var Q3;
            Q3=makeQuery(id+"F39.opExtrude","CAP_EDGE",EDGE,{"disambiguationData":[OSD([sQuery(id+"F37.wireOp",EDGE,"E29.bottom")])],"isStart":false});
            fillet(context, id + "F40", {"entities" : qUnion([Q0, Q1, Q2, Q3]), "radius" : 50 * mm, "tangentPropagation" : true, "allowEdgeOverflow" : false});
        }
    });
